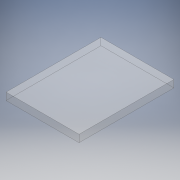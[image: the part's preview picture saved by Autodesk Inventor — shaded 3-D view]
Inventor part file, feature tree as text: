
AUTODESK INVENTOR PART (.ipt)
format: ipt  version: 2017 (Build 210142000, 142)  size: 93,696 bytes
history: native  units: mm
features: extrude x1, sketch x1
ambient origin geometry x8: Origin, YZ Plane, XZ Plane, XY Plane, X Axis, Y Axis, Z Axis, Center Point
bodies: Solid1 (feature_tree)
feature tree (2):
  extrude  "Extrusion1"  Depth=130.0mm
  sketch  "Sketch1"  dims[d0=100.0mm d1=130.0mm d2=10.0mm d3=0.0mm]
